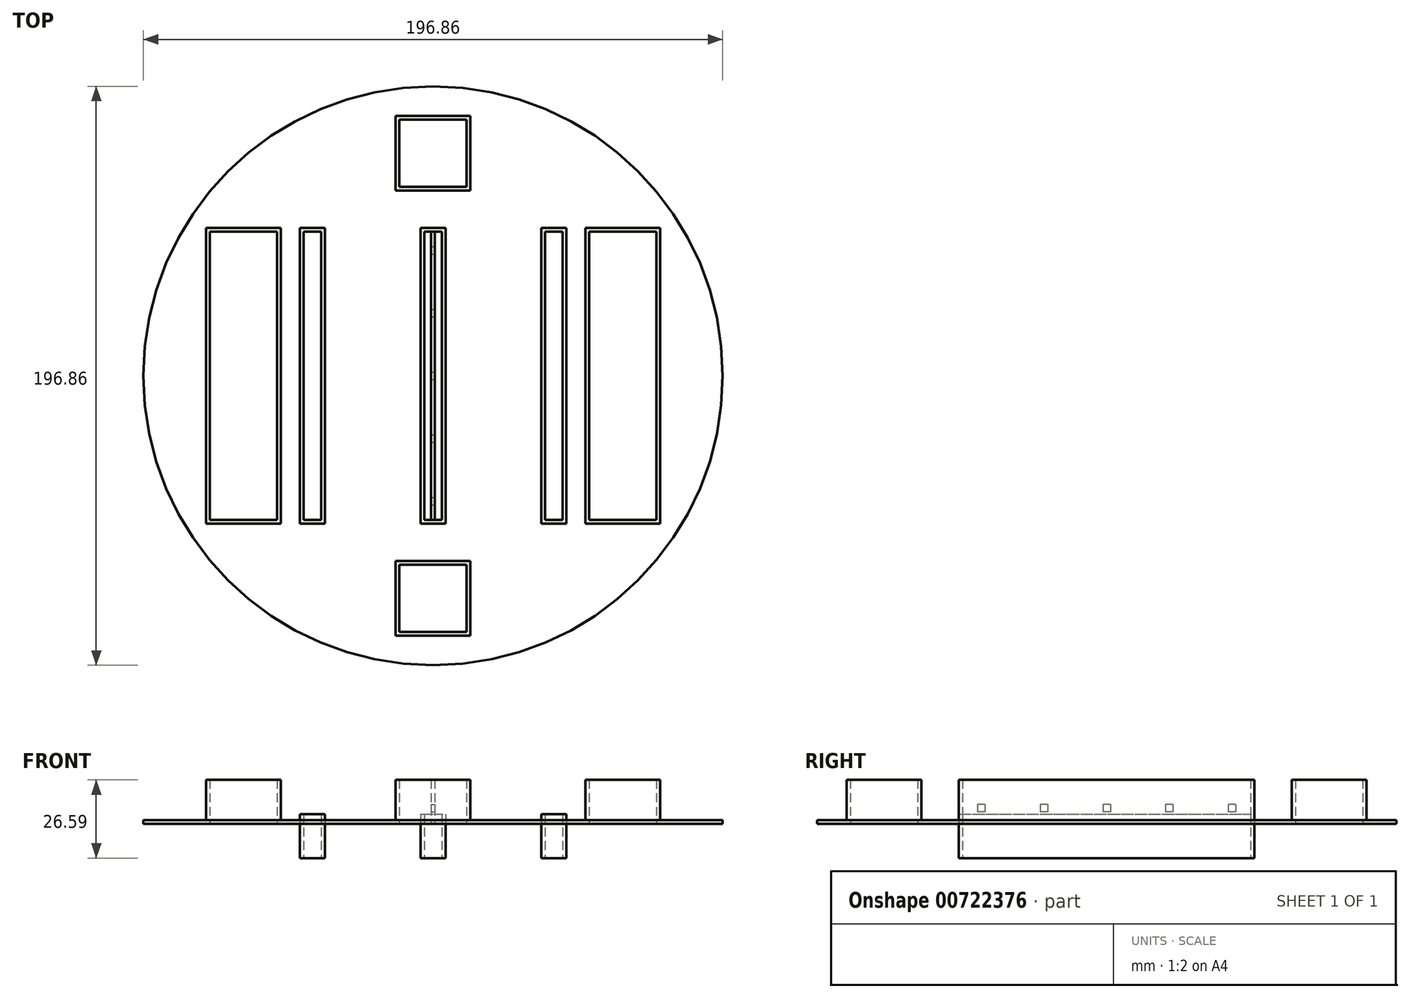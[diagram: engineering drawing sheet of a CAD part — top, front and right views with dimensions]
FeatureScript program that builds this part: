
annotation { "Feature Type Name" : "Feature", "Feature Type Description" : "" }
export const myFeature = defineFeature(function(context is Context, id is Id, definition is map)
    precondition{}
    {
        {
            var Q0;
            Q0=qCreatedBy(makeId("Top.planeOp"),FACE);
            var sketch = newSketch(context, id + "F0", { "sketchPlane" : qUnion([Q0])});
            skCircle(sketch, "E0", {"center": v(0, 0) * mm, "radius": 98.43 * mm});
            skLineSegment(sketch, "E1", {"start": v(0, 98.43) * mm, "end": v(0, -98.43) * mm, "construction": true});
            skLineSegment(sketch, "E2", {"start": v(-98.43, 0) * mm, "end": v(98.43, 0) * mm, "construction": true});
            skLineSegment(sketch, "E3", {"start": v(0, 0) * mm, "end": v(0, 75.67) * mm, "construction": true});
            skLineSegment(sketch, "E4", {"start": v(0, 0) * mm, "end": v(0, -75.67) * mm, "construction": true});
            skLineSegment(sketch, "E5", {"start": v(0, 0) * mm, "end": v(-64.43, 0) * mm, "construction": true});
            skLineSegment(sketch, "E6", {"start": v(0, 0) * mm, "end": v(64.43, 0) * mm, "construction": true});
            skLineSegment(sketch, "E7", {"start": v(0, 0) * mm, "end": v(-41.01, 0) * mm, "construction": true});
            skLineSegment(sketch, "E8", {"start": v(0, 0) * mm, "end": v(41.01, 0) * mm, "construction": true});
            skLineSegment(sketch, "E9.bottom", {"start": v(77.13, -50.27) * mm, "end": v(51.73, -50.27) * mm});
            skLineSegment(sketch, "E9.top", {"start": v(77.13, 50.27) * mm, "end": v(51.73, 50.27) * mm});
            skLineSegment(sketch, "E9.left", {"start": v(77.13, -50.27) * mm, "end": v(77.13, 50.27) * mm});
            skLineSegment(sketch, "E9.right", {"start": v(51.73, -50.27) * mm, "end": v(51.73, 50.27) * mm});
            skPoint(sketch, "E9.middle", {"position": v(64.43, 0) * mm});
            skLineSegment(sketch, "E10.bottom", {"start": v(-51.73, -50.27) * mm, "end": v(-77.13, -50.27) * mm});
            skLineSegment(sketch, "E10.top", {"start": v(-51.73, 50.27) * mm, "end": v(-77.13, 50.27) * mm});
            skLineSegment(sketch, "E10.left", {"start": v(-51.73, -50.27) * mm, "end": v(-51.73, 50.27) * mm});
            skLineSegment(sketch, "E10.right", {"start": v(-77.13, -50.27) * mm, "end": v(-77.13, 50.27) * mm});
            skPoint(sketch, "E10.middle", {"position": v(-64.43, 0) * mm});
            skLineSegment(sketch, "E11.bottom", {"start": v(-12.7, 62.97) * mm, "end": v(12.7, 62.97) * mm});
            skLineSegment(sketch, "E11.top", {"start": v(-12.7, 88.37) * mm, "end": v(12.7, 88.37) * mm});
            skLineSegment(sketch, "E11.left", {"start": v(-12.7, 62.97) * mm, "end": v(-12.7, 88.37) * mm});
            skLineSegment(sketch, "E11.right", {"start": v(12.7, 62.97) * mm, "end": v(12.7, 88.37) * mm});
            skPoint(sketch, "E11.middle", {"position": v(0, 75.67) * mm});
            skLineSegment(sketch, "E12.bottom", {"start": v(-12.7, -88.37) * mm, "end": v(12.7, -88.37) * mm});
            skLineSegment(sketch, "E12.top", {"start": v(-12.7, -62.97) * mm, "end": v(12.7, -62.97) * mm});
            skLineSegment(sketch, "E12.left", {"start": v(-12.7, -88.37) * mm, "end": v(-12.7, -62.97) * mm});
            skLineSegment(sketch, "E12.right", {"start": v(12.7, -88.37) * mm, "end": v(12.7, -62.97) * mm});
            skPoint(sketch, "E12.middle", {"position": v(0, -75.67) * mm});
            skLineSegment(sketch, "E13.bottom", {"start": v(36.78, -50.27) * mm, "end": v(45.24, -50.27) * mm});
            skLineSegment(sketch, "E13.top", {"start": v(36.78, 50.27) * mm, "end": v(45.24, 50.27) * mm});
            skLineSegment(sketch, "E13.left", {"start": v(36.78, -50.27) * mm, "end": v(36.78, 50.27) * mm});
            skLineSegment(sketch, "E13.right", {"start": v(45.24, -50.27) * mm, "end": v(45.24, 50.27) * mm});
            skPoint(sketch, "E13.middle", {"position": v(41.01, 0) * mm});
            skLineSegment(sketch, "E14.bottom", {"start": v(-4.23, -50.27) * mm, "end": v(4.23, -50.27) * mm});
            skLineSegment(sketch, "E14.top", {"start": v(-4.23, 50.27) * mm, "end": v(4.23, 50.27) * mm});
            skLineSegment(sketch, "E14.left", {"start": v(-4.23, -50.27) * mm, "end": v(-4.23, 50.27) * mm});
            skLineSegment(sketch, "E14.right", {"start": v(4.23, -50.27) * mm, "end": v(4.23, 50.27) * mm});
            skLineSegment(sketch, "E15.bottom", {"start": v(-45.24, -50.27) * mm, "end": v(-36.78, -50.27) * mm});
            skLineSegment(sketch, "E15.top", {"start": v(-45.24, 50.27) * mm, "end": v(-36.78, 50.27) * mm});
            skLineSegment(sketch, "E15.left", {"start": v(-45.24, -50.27) * mm, "end": v(-45.24, 50.27) * mm});
            skLineSegment(sketch, "E15.right", {"start": v(-36.78, -50.27) * mm, "end": v(-36.78, 50.27) * mm});
            skPoint(sketch, "E15.middle", {"position": v(-41.01, 0) * mm});
            skSolve(sketch);
        }
        {
            var Q0;
            Q0 = qSketchRegion(id + "F0", true);
            extrude(context, id + "F1", {"entities" : qUnion([Q0]), "depth" : 1.27 * mm, "offsetDistance" : 25.4 * mm});
        }
        {
            var Q0;
            Q0=makeQuery(id+"F0.imprint","IMPRINT",FACE,{"disambiguationData":[TD([[makeQuery(id+"F0.imprint","IMPRINT",EDGE,{"derivedFrom":sQuery(id+"F0.wireOp",EDGE,"E11.bottom")}),1.0]])]});
            var Q1;
            Q1=makeQuery(id+"F0.imprint","IMPRINT",FACE,{"disambiguationData":[TD([[makeQuery(id+"F0.imprint","IMPRINT",EDGE,{"derivedFrom":sQuery(id+"F0.wireOp",EDGE,"E10.bottom")}),-1.0]])]});
            var Q2;
            Q2=makeQuery(id+"F0.imprint","IMPRINT",FACE,{"disambiguationData":[TD([[makeQuery(id+"F0.imprint","IMPRINT",EDGE,{"derivedFrom":sQuery(id+"F0.wireOp",EDGE,"E9.bottom")}),-1.0]])]});
            var Q3;
            Q3=makeQuery(id+"F0.imprint","IMPRINT",FACE,{"disambiguationData":[TD([[makeQuery(id+"F0.imprint","IMPRINT",EDGE,{"derivedFrom":sQuery(id+"F0.wireOp",EDGE,"E12.bottom")}),1.0]])]});
            extrude(context, id + "F2", {"entities" : qUnion([Q0, Q1, Q2, Q3]), "operationType" : NewBodyOperationType.ADD, "depth" : 14.95 * mm, "offsetDistance" : 25.4 * mm});
        }
        {
            var Q0;
            Q0=makeQuery(id+"F2.opExtrude","CAP_FACE",FACE,{"disambiguationData":[OSD([sQuery(id+"F0.wireOp",EDGE,"E10.bottom"),sQuery(id+"F0.wireOp",EDGE,"E10.top"),sQuery(id+"F0.wireOp",EDGE,"E10.left"),sQuery(id+"F0.wireOp",EDGE,"E10.right")])],"isStart":false});
            var Q1;
            Q1=makeQuery(id+"F2.opExtrude","CAP_FACE",FACE,{"disambiguationData":[OSD([sQuery(id+"F0.wireOp",EDGE,"E11.bottom"),sQuery(id+"F0.wireOp",EDGE,"E11.top"),sQuery(id+"F0.wireOp",EDGE,"E11.left"),sQuery(id+"F0.wireOp",EDGE,"E11.right")])],"isStart":false});
            var Q2;
            Q2=makeQuery(id+"F2.opExtrude","CAP_FACE",FACE,{"disambiguationData":[OSD([sQuery(id+"F0.wireOp",EDGE,"E9.bottom"),sQuery(id+"F0.wireOp",EDGE,"E9.top"),sQuery(id+"F0.wireOp",EDGE,"E9.left"),sQuery(id+"F0.wireOp",EDGE,"E9.right")])],"isStart":false});
            var Q3;
            Q3=makeQuery(id+"F2.opExtrude","CAP_FACE",FACE,{"disambiguationData":[OSD([sQuery(id+"F0.wireOp",EDGE,"E12.bottom"),sQuery(id+"F0.wireOp",EDGE,"E12.top"),sQuery(id+"F0.wireOp",EDGE,"E12.left"),sQuery(id+"F0.wireOp",EDGE,"E12.right")])],"isStart":false});
            shell(context, id + "F3", {"entities" : qUnion([Q0, Q1, Q2, Q3]), "thickness" : 1.27 * mm});
        }
        {
            var Q0;
            Q0=makeQuery(id+"F3.opShell","OFFSET_FACE",FACE,{"disambiguationData":[OSD([sQuery(id+"F0.wireOp",EDGE,"E0"),sQuery(id+"F0.wireOp",EDGE,"E9.bottom"),sQuery(id+"F0.wireOp",EDGE,"E9.top"),sQuery(id+"F0.wireOp",EDGE,"E9.left"),sQuery(id+"F0.wireOp",EDGE,"E9.right"),sQuery(id+"F0.wireOp",EDGE,"E10.bottom"),sQuery(id+"F0.wireOp",EDGE,"E10.top"),sQuery(id+"F0.wireOp",EDGE,"E10.left"),sQuery(id+"F0.wireOp",EDGE,"E10.right"),sQuery(id+"F0.wireOp",EDGE,"E11.bottom"),sQuery(id+"F0.wireOp",EDGE,"E11.top"),sQuery(id+"F0.wireOp",EDGE,"E11.left"),sQuery(id+"F0.wireOp",EDGE,"E11.right"),sQuery(id+"F0.wireOp",EDGE,"E12.bottom"),sQuery(id+"F0.wireOp",EDGE,"E12.top"),sQuery(id+"F0.wireOp",EDGE,"E12.left"),sQuery(id+"F0.wireOp",EDGE,"E12.right"),sQuery(id+"F0.wireOp",EDGE,"E13.bottom"),sQuery(id+"F0.wireOp",EDGE,"E13.top"),sQuery(id+"F0.wireOp",EDGE,"E13.left"),sQuery(id+"F0.wireOp",EDGE,"E13.right"),sQuery(id+"F0.wireOp",EDGE,"E14.bottom"),sQuery(id+"F0.wireOp",EDGE,"E14.top"),sQuery(id+"F0.wireOp",EDGE,"E14.left"),sQuery(id+"F0.wireOp",EDGE,"E14.right"),sQuery(id+"F0.wireOp",EDGE,"E15.bottom"),sQuery(id+"F0.wireOp",EDGE,"E15.top"),sQuery(id+"F0.wireOp",EDGE,"E15.left"),sQuery(id+"F0.wireOp",EDGE,"E15.right")]),OD(1.0)]});
            var Q1;
            Q1=makeQuery(id+"F3.opShell","OFFSET_FACE",FACE,{"disambiguationData":[OSD([sQuery(id+"F0.wireOp",EDGE,"E0"),sQuery(id+"F0.wireOp",EDGE,"E9.bottom"),sQuery(id+"F0.wireOp",EDGE,"E9.top"),sQuery(id+"F0.wireOp",EDGE,"E9.left"),sQuery(id+"F0.wireOp",EDGE,"E9.right"),sQuery(id+"F0.wireOp",EDGE,"E10.bottom"),sQuery(id+"F0.wireOp",EDGE,"E10.top"),sQuery(id+"F0.wireOp",EDGE,"E10.left"),sQuery(id+"F0.wireOp",EDGE,"E10.right"),sQuery(id+"F0.wireOp",EDGE,"E11.bottom"),sQuery(id+"F0.wireOp",EDGE,"E11.top"),sQuery(id+"F0.wireOp",EDGE,"E11.left"),sQuery(id+"F0.wireOp",EDGE,"E11.right"),sQuery(id+"F0.wireOp",EDGE,"E12.bottom"),sQuery(id+"F0.wireOp",EDGE,"E12.top"),sQuery(id+"F0.wireOp",EDGE,"E12.left"),sQuery(id+"F0.wireOp",EDGE,"E12.right"),sQuery(id+"F0.wireOp",EDGE,"E13.bottom"),sQuery(id+"F0.wireOp",EDGE,"E13.top"),sQuery(id+"F0.wireOp",EDGE,"E13.left"),sQuery(id+"F0.wireOp",EDGE,"E13.right"),sQuery(id+"F0.wireOp",EDGE,"E14.bottom"),sQuery(id+"F0.wireOp",EDGE,"E14.top"),sQuery(id+"F0.wireOp",EDGE,"E14.left"),sQuery(id+"F0.wireOp",EDGE,"E14.right"),sQuery(id+"F0.wireOp",EDGE,"E15.bottom"),sQuery(id+"F0.wireOp",EDGE,"E15.top"),sQuery(id+"F0.wireOp",EDGE,"E15.left"),sQuery(id+"F0.wireOp",EDGE,"E15.right")]),OD(2.0)]});
            var Q2;
            Q2=makeQuery(id+"F3.opShell","OFFSET_FACE",FACE,{"disambiguationData":[OSD([sQuery(id+"F0.wireOp",EDGE,"E0"),sQuery(id+"F0.wireOp",EDGE,"E9.bottom"),sQuery(id+"F0.wireOp",EDGE,"E9.top"),sQuery(id+"F0.wireOp",EDGE,"E9.left"),sQuery(id+"F0.wireOp",EDGE,"E9.right"),sQuery(id+"F0.wireOp",EDGE,"E10.bottom"),sQuery(id+"F0.wireOp",EDGE,"E10.top"),sQuery(id+"F0.wireOp",EDGE,"E10.left"),sQuery(id+"F0.wireOp",EDGE,"E10.right"),sQuery(id+"F0.wireOp",EDGE,"E11.bottom"),sQuery(id+"F0.wireOp",EDGE,"E11.top"),sQuery(id+"F0.wireOp",EDGE,"E11.left"),sQuery(id+"F0.wireOp",EDGE,"E11.right"),sQuery(id+"F0.wireOp",EDGE,"E12.bottom"),sQuery(id+"F0.wireOp",EDGE,"E12.top"),sQuery(id+"F0.wireOp",EDGE,"E12.left"),sQuery(id+"F0.wireOp",EDGE,"E12.right"),sQuery(id+"F0.wireOp",EDGE,"E13.bottom"),sQuery(id+"F0.wireOp",EDGE,"E13.top"),sQuery(id+"F0.wireOp",EDGE,"E13.left"),sQuery(id+"F0.wireOp",EDGE,"E13.right"),sQuery(id+"F0.wireOp",EDGE,"E14.bottom"),sQuery(id+"F0.wireOp",EDGE,"E14.top"),sQuery(id+"F0.wireOp",EDGE,"E14.left"),sQuery(id+"F0.wireOp",EDGE,"E14.right"),sQuery(id+"F0.wireOp",EDGE,"E15.bottom"),sQuery(id+"F0.wireOp",EDGE,"E15.top"),sQuery(id+"F0.wireOp",EDGE,"E15.left"),sQuery(id+"F0.wireOp",EDGE,"E15.right")]),OD(0.0)]});
            var Q3;
            Q3=makeQuery(id+"F3.opShell","OFFSET_FACE",FACE,{"disambiguationData":[OSD([sQuery(id+"F0.wireOp",EDGE,"E0"),sQuery(id+"F0.wireOp",EDGE,"E9.bottom"),sQuery(id+"F0.wireOp",EDGE,"E9.top"),sQuery(id+"F0.wireOp",EDGE,"E9.left"),sQuery(id+"F0.wireOp",EDGE,"E9.right"),sQuery(id+"F0.wireOp",EDGE,"E10.bottom"),sQuery(id+"F0.wireOp",EDGE,"E10.top"),sQuery(id+"F0.wireOp",EDGE,"E10.left"),sQuery(id+"F0.wireOp",EDGE,"E10.right"),sQuery(id+"F0.wireOp",EDGE,"E11.bottom"),sQuery(id+"F0.wireOp",EDGE,"E11.top"),sQuery(id+"F0.wireOp",EDGE,"E11.left"),sQuery(id+"F0.wireOp",EDGE,"E11.right"),sQuery(id+"F0.wireOp",EDGE,"E12.bottom"),sQuery(id+"F0.wireOp",EDGE,"E12.top"),sQuery(id+"F0.wireOp",EDGE,"E12.left"),sQuery(id+"F0.wireOp",EDGE,"E12.right"),sQuery(id+"F0.wireOp",EDGE,"E13.bottom"),sQuery(id+"F0.wireOp",EDGE,"E13.top"),sQuery(id+"F0.wireOp",EDGE,"E13.left"),sQuery(id+"F0.wireOp",EDGE,"E13.right"),sQuery(id+"F0.wireOp",EDGE,"E14.bottom"),sQuery(id+"F0.wireOp",EDGE,"E14.top"),sQuery(id+"F0.wireOp",EDGE,"E14.left"),sQuery(id+"F0.wireOp",EDGE,"E14.right"),sQuery(id+"F0.wireOp",EDGE,"E15.bottom"),sQuery(id+"F0.wireOp",EDGE,"E15.top"),sQuery(id+"F0.wireOp",EDGE,"E15.left"),sQuery(id+"F0.wireOp",EDGE,"E15.right")]),OD(3.0)]});
            extrude(context, id + "F4", {"entities" : qUnion([Q0, Q1, Q2, Q3]), "operationType" : NewBodyOperationType.REMOVE, "oppositeDirection" : true, "depth" : 25.4 * mm, "offsetDistance" : 25.4 * mm});
        }
        {
            var Q0;
            Q0=makeQuery(id+"F0.imprint","IMPRINT",FACE,{"disambiguationData":[TD([[makeQuery(id+"F0.imprint","IMPRINT",EDGE,{"derivedFrom":sQuery(id+"F0.wireOp",EDGE,"E15.bottom")}),1.0]])]});
            var Q1;
            Q1=makeQuery(id+"F0.imprint","IMPRINT",FACE,{"disambiguationData":[TD([[makeQuery(id+"F0.imprint","IMPRINT",EDGE,{"derivedFrom":sQuery(id+"F0.wireOp",EDGE,"E14.bottom")}),1.0]])]});
            var Q2;
            Q2=makeQuery(id+"F0.imprint","IMPRINT",FACE,{"disambiguationData":[TD([[makeQuery(id+"F0.imprint","IMPRINT",EDGE,{"derivedFrom":sQuery(id+"F0.wireOp",EDGE,"E13.bottom")}),1.0]])]});
            extrude(context, id + "F5", {"entities" : qUnion([Q0, Q1, Q2]), "depth" : 3.3 * mm, "offsetDistance" : 25.4 * mm, "hasSecondDirection" : true, "secondDirectionOppositeDirection" : true, "secondDirectionDepth" : 11.64 * mm});
        }
        {
            var Q0;
            Q0=makeQuery(id+"F5.opExtrude","CAP_FACE",FACE,{"disambiguationData":[OSD([sQuery(id+"F0.wireOp",EDGE,"E15.bottom"),sQuery(id+"F0.wireOp",EDGE,"E15.top"),sQuery(id+"F0.wireOp",EDGE,"E15.left"),sQuery(id+"F0.wireOp",EDGE,"E15.right")])],"isStart":false});
            var Q1;
            Q1=makeQuery(id+"F5.opExtrude","CAP_FACE",FACE,{"disambiguationData":[OSD([sQuery(id+"F0.wireOp",EDGE,"E14.bottom"),sQuery(id+"F0.wireOp",EDGE,"E14.top"),sQuery(id+"F0.wireOp",EDGE,"E14.left"),sQuery(id+"F0.wireOp",EDGE,"E14.right")])],"isStart":false});
            var Q2;
            Q2=makeQuery(id+"F5.opExtrude","CAP_FACE",FACE,{"disambiguationData":[OSD([sQuery(id+"F0.wireOp",EDGE,"E13.bottom"),sQuery(id+"F0.wireOp",EDGE,"E13.top"),sQuery(id+"F0.wireOp",EDGE,"E13.left"),sQuery(id+"F0.wireOp",EDGE,"E13.right")])],"isStart":false});
            shell(context, id + "F6", {"entities" : qUnion([Q0, Q1, Q2]), "thickness" : 1.27 * mm});
        }
        {
            var Q0;
            Q0=makeQuery(id+"F6.opShell","OFFSET_FACE",FACE,{"disambiguationData":[OSD([sQuery(id+"F0.wireOp",EDGE,"E15.bottom"),sQuery(id+"F0.wireOp",EDGE,"E15.top"),sQuery(id+"F0.wireOp",EDGE,"E15.left"),sQuery(id+"F0.wireOp",EDGE,"E15.right")])]});
            var Q1;
            Q1=makeQuery(id+"F6.opShell","OFFSET_FACE",FACE,{"disambiguationData":[OSD([sQuery(id+"F0.wireOp",EDGE,"E14.bottom"),sQuery(id+"F0.wireOp",EDGE,"E14.top"),sQuery(id+"F0.wireOp",EDGE,"E14.left"),sQuery(id+"F0.wireOp",EDGE,"E14.right")])]});
            var Q2;
            Q2=makeQuery(id+"F6.opShell","OFFSET_FACE",FACE,{"disambiguationData":[OSD([sQuery(id+"F0.wireOp",EDGE,"E13.bottom"),sQuery(id+"F0.wireOp",EDGE,"E13.top"),sQuery(id+"F0.wireOp",EDGE,"E13.left"),sQuery(id+"F0.wireOp",EDGE,"E13.right")])]});
            extrude(context, id + "F7", {"entities" : qUnion([Q0, Q1, Q2]), "operationType" : NewBodyOperationType.REMOVE, "oppositeDirection" : true, "depth" : 25.4 * mm, "offsetDistance" : 25.4 * mm});
        }
        {
            var Q0;
            Q0=qCreatedBy(makeId("Right.planeOp"),FACE);
            var sketch = newSketch(context, id + "F8", { "sketchPlane" : qUnion([Q0])});
            skLineSegment(sketch, "E16", {"start": v(0, 0) * mm, "end": v(0, 7.47) * mm, "construction": true});
            skLineSegment(sketch, "E17.bottom", {"start": v(49, 14.95) * mm, "end": v(-49, 14.95) * mm});
            skLineSegment(sketch, "E17.top", {"start": v(49, 0) * mm, "end": v(-49, 0) * mm});
            skLineSegment(sketch, "E17.left", {"start": v(49, 14.95) * mm, "end": v(49, 0) * mm});
            skLineSegment(sketch, "E17.right", {"start": v(-49, 14.95) * mm, "end": v(-49, 0) * mm});
            skPoint(sketch, "E17.middle", {"position": v(0, 7.47) * mm});
            skSolve(sketch);
        }
        {
            var Q0;
            Q0 = qSketchRegion(id + "F8", true);
            extrude(context, id + "F9", {"entities" : qUnion([Q0]), "depth" : 0.64 * mm, "offsetDistance" : 25.4 * mm, "hasSecondDirection" : true, "secondDirectionOppositeDirection" : true, "secondDirectionDepth" : 0.64 * mm});
        }
        {
            var Q0;
            Q0=qCreatedBy(makeId("Right.planeOp"),FACE);
            var sketch = newSketch(context, id + "F10", { "sketchPlane" : qUnion([Q0])});
            skLineSegment(sketch, "E18", {"start": v(0, 0) * mm, "end": v(-49, 0) * mm, "construction": true});
            skLineSegment(sketch, "E19", {"start": v(0, 0) * mm, "end": v(49, 0) * mm, "construction": true});
            skLineSegment(sketch, "E20", {"start": v(0, 0) * mm, "end": v(-21.33, 0) * mm, "construction": true});
            skLineSegment(sketch, "E21", {"start": v(0, 0) * mm, "end": v(21.33, 0) * mm, "construction": true});
            skLineSegment(sketch, "E22", {"start": v(-49, 0) * mm, "end": v(-42.65, 0) * mm, "construction": true});
            skLineSegment(sketch, "E23", {"start": v(-42.65, 0) * mm, "end": v(-21.33, 0) * mm, "construction": true});
            skLineSegment(sketch, "E24", {"start": v(21.33, 0) * mm, "end": v(42.65, 0) * mm, "construction": true});
            skLineSegment(sketch, "E25", {"start": v(42.65, 0) * mm, "end": v(49, 0) * mm, "construction": true});
            skLineSegment(sketch, "E26", {"start": v(-42.65, 0) * mm, "end": v(-42.65, 5.3) * mm, "construction": true});
            skLineSegment(sketch, "E27", {"start": v(-21.33, 0) * mm, "end": v(-21.33, 5.3) * mm, "construction": true});
            skLineSegment(sketch, "E28", {"start": v(0, 0) * mm, "end": v(0, 5.3) * mm, "construction": true});
            skLineSegment(sketch, "E29", {"start": v(21.33, 0) * mm, "end": v(21.33, 5.3) * mm, "construction": true});
            skLineSegment(sketch, "E30", {"start": v(42.65, 0) * mm, "end": v(42.65, 5.3) * mm, "construction": true});
            skLineSegment(sketch, "E31.bottom", {"start": v(-41.38, 6.56) * mm, "end": v(-43.92, 6.56) * mm});
            skLineSegment(sketch, "E31.top", {"start": v(-41.38, 4.02) * mm, "end": v(-43.92, 4.02) * mm});
            skLineSegment(sketch, "E31.left", {"start": v(-41.38, 6.56) * mm, "end": v(-41.38, 4.02) * mm});
            skLineSegment(sketch, "E31.right", {"start": v(-43.92, 6.56) * mm, "end": v(-43.92, 4.02) * mm});
            skPoint(sketch, "E31.middle", {"position": v(-42.65, 5.3) * mm});
            skLineSegment(sketch, "E32.bottom", {"start": v(-20.06, 6.56) * mm, "end": v(-22.6, 6.56) * mm});
            skLineSegment(sketch, "E32.top", {"start": v(-20.06, 4.02) * mm, "end": v(-22.6, 4.02) * mm});
            skLineSegment(sketch, "E32.left", {"start": v(-20.06, 6.56) * mm, "end": v(-20.06, 4.02) * mm});
            skLineSegment(sketch, "E32.right", {"start": v(-22.6, 6.56) * mm, "end": v(-22.6, 4.02) * mm});
            skPoint(sketch, "E32.middle", {"position": v(-21.33, 5.3) * mm});
            skLineSegment(sketch, "E33.bottom", {"start": v(1.27, 6.56) * mm, "end": v(-1.27, 6.56) * mm});
            skLineSegment(sketch, "E33.top", {"start": v(1.27, 4.02) * mm, "end": v(-1.27, 4.02) * mm});
            skLineSegment(sketch, "E33.left", {"start": v(1.27, 6.56) * mm, "end": v(1.27, 4.02) * mm});
            skLineSegment(sketch, "E33.right", {"start": v(-1.27, 6.56) * mm, "end": v(-1.27, 4.02) * mm});
            skPoint(sketch, "E33.middle", {"position": v(0, 5.3) * mm});
            skLineSegment(sketch, "E34.bottom", {"start": v(22.6, 6.56) * mm, "end": v(20.06, 6.56) * mm});
            skLineSegment(sketch, "E34.top", {"start": v(22.6, 4.02) * mm, "end": v(20.06, 4.02) * mm});
            skLineSegment(sketch, "E34.left", {"start": v(22.6, 6.56) * mm, "end": v(22.6, 4.02) * mm});
            skLineSegment(sketch, "E34.right", {"start": v(20.06, 6.56) * mm, "end": v(20.06, 4.02) * mm});
            skPoint(sketch, "E34.middle", {"position": v(21.33, 5.3) * mm});
            skLineSegment(sketch, "E35.bottom", {"start": v(43.92, 6.56) * mm, "end": v(41.38, 6.56) * mm});
            skLineSegment(sketch, "E35.top", {"start": v(43.92, 4.02) * mm, "end": v(41.38, 4.02) * mm});
            skLineSegment(sketch, "E35.left", {"start": v(43.92, 6.56) * mm, "end": v(43.92, 4.02) * mm});
            skLineSegment(sketch, "E35.right", {"start": v(41.38, 6.56) * mm, "end": v(41.38, 4.02) * mm});
            skPoint(sketch, "E35.middle", {"position": v(42.65, 5.3) * mm});
            skSolve(sketch);
        }
        {
            var Q0;
            Q0 = qSketchRegion(id + "F10", true);
            extrude(context, id + "F11", {"entities" : qUnion([Q0]), "operationType" : NewBodyOperationType.REMOVE, "oppositeDirection" : true, "depth" : 25.4 * mm, "offsetDistance" : 25.4 * mm, "hasSecondDirection" : true, "secondDirectionOppositeDirection" : false, "secondDirectionDepth" : 25.4 * mm});
        }
    });
